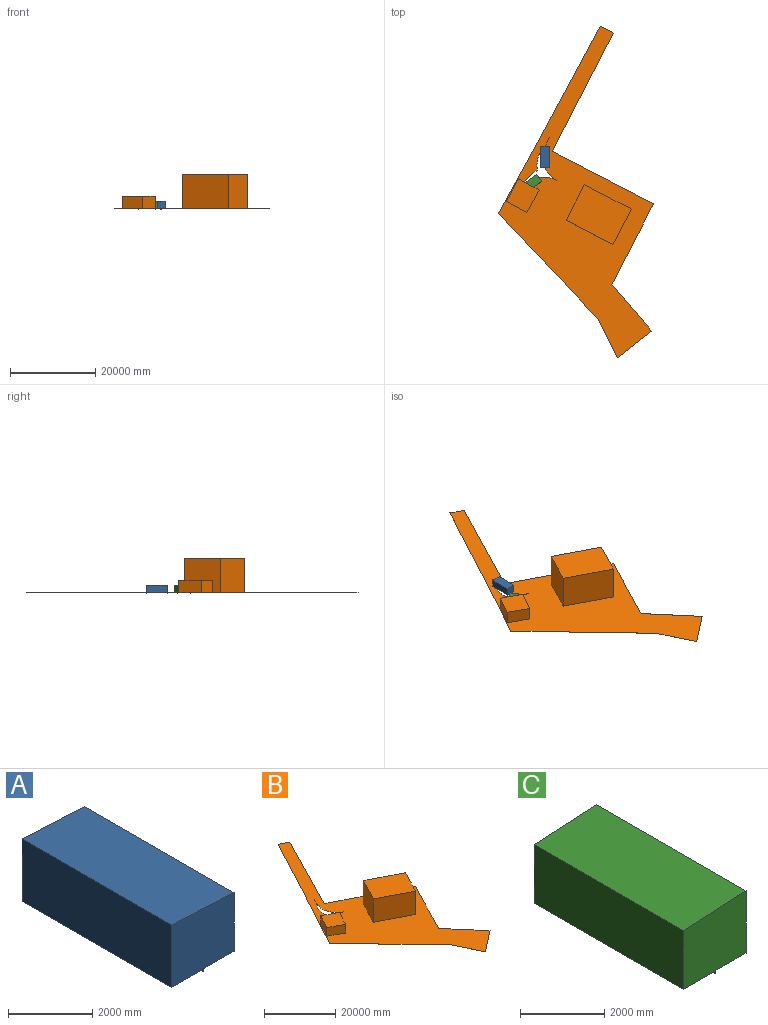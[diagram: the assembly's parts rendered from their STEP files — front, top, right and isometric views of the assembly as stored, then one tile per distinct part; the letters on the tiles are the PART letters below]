
ASSEMBLY  parts=3 mates=2
PART A: 12 faces, bbox 2100x5020x1860.1 mm
  f0: plane 2100x1810.06mm, normal (0,-1,0), area 3685559.2mm2, adj f1,f3,f4,f5,f6
  f1: plane 5000x1700mm, normal (1,0,0), area 8500000mm2, adj f0,f2,f4,f5
  f2: plane 2100x1810.06mm, normal (0,1,0), area 3685559.2mm2, adj f1,f3,f4,f5,f11
  f3: plane 5000x1810.06mm, normal (-1,0,0), area 9050281.7mm2, adj f0,f2,f4,f5
  f4: plane 5000x2100mm, normal (0.05,0,1), area 10514409.6mm2, adj f0,f1,f2,f3
  f5: plane 5000x2100mm, normal (0,0,-1), area 10499685.8mm2, adj f0,f1,f2,f3,f7,f9
  f6: plane 20x10mm, normal (0,0,1), area 157.1mm2, adj f0,f7
  f7: cylinder r=10mm len=50mm, axis (0,0,1), area 3141.6mm2, adj f5,f6,f8
  f8: plane 20x20mm, normal (0,0,-1), area 314.2mm2, adj f7
  f9: cylinder r=10mm len=50mm, axis (0,0,1), area 3141.6mm2, adj f5,f10,f11
  f10: plane 20x20mm, normal (0,0,-1), area 314.2mm2, adj f9
  f11: plane 20x10mm, normal (0,0,1), area 157.1mm2, adj f2,f9
PART B: 36 faces, bbox 36480.2x78044.6x8005 mm
  f0: plane 78044.58x36480.23mm, normal (0,0,1), area 819877426.7mm2, adj f2,f3,f4,f5,f6,f7,f8,f9
  f1: plane 78044.58x36480.23mm, normal (0,0,-1), area 968303998.2mm2, adj f2,f3,f4,f5,f6,f7,f8,f9
  f2: plane 27682.43x14769.46mm, normal (-0.88,0.47,0), area 156880mm2, adj f0,f1,f3,f11
  f3: plane 16564.67x9013.23mm, normal (-0.88,0.48,0), area 94290.3mm2, adj f0,f1,f2,f4
  f4: plane 24646.07x23560.1mm, normal (-0.72,-0.69,0), area 170477.8mm2, adj f0,f1,f3,f5
  f5: plane 9151.42x4420.6mm, normal (-0.9,-0.43,0), area 50815.9mm2, adj f0,f1,f4,f6
  f6: plane 8143.21x6359.46mm, normal (0.62,-0.79,0), area 51661.1mm2, adj f0,f1,f5,f7
  f7: plane 10935.17x9384.08mm, normal (0.76,0.65,0), area 72048.4mm2, adj f0,f1,f6,f8
  f8: plane 18967.71x9740.4mm, normal (0.89,-0.46,0), area 106612.6mm2, adj f0,f1,f7,f9
  f9: plane 23911.22x12274.5mm, normal (0.46,0.89,0), area 134388.4mm2, adj f0,f1,f8,f10
  f10: plane 27860.2x14301.66mm, normal (0.89,-0.46,0), area 156582.9mm2, adj f0,f1,f9,f11
  f11: plane 3087.98x1647.54mm, normal (0.47,0.88,0), area 17500mm2, adj f0,f1,f2,f10
  f12: plane 5270.32x3000mm, normal (0.88,-0.48,0), area 18000000mm2, adj f0,f13,f15,f16
  f13: plane 4831.13x3000mm, normal (0.48,0.88,0), area 16500000mm2, adj f0,f12,f14,f16,f27
  f14: plane 5270.32x3000mm, normal (-0.88,0.48,0), area 18000000mm2, adj f0,f13,f15,f16
  f15: plane 4831.13x3000mm, normal (-0.48,-0.88,0), area 16500000mm2, adj f0,f12,f14,f16
  f16: plane 7899.05x7698.83mm, normal (0,0,1), area 33000000mm2, adj f12,f13,f14,f15
  f17: plane 8341.3x8000mm, normal (0.89,-0.46,0), area 75014828.3mm2, adj f0,f18,f20,f21
  f18: plane 11032.67x8000mm, normal (0.46,0.89,0), area 99211211.4mm2, adj f0,f17,f19,f21
  f19: plane 8340.29x8000mm, normal (-0.89,0.46,0), area 75000000mm2, adj f0,f18,f20,f21
  f20: plane 11030.58x8000mm, normal (-0.46,-0.89,0), area 99200000mm2, adj f0,f17,f19,f21
  f21: plane 15314.05x14004.77mm, normal (0,0,1), area 116268061.2mm2, adj f17,f18,f19,f20
  f22: cylinder r=6000mm len=8010.4mm, axis (0,0,1), area 46402.1mm2, adj f0,f1,f23,f27,f28
  f23: plane 2034.22x1106.87mm, normal (-0.88,0.48,0), area 11579.3mm2, adj f1,f22,f24,f27
  f24: plane 17.57x9.56mm, normal (0.48,0.88,0), area 100mm2, adj f1,f23,f25,f27
  f25: plane 2034.22x1106.87mm, normal (0.88,-0.48,0), area 11579.3mm2, adj f1,f24,f26,f27
  f26: cylinder r=6000mm len=4748.25mm, axis (0,0,1), area 31154.3mm2, adj f0,f1,f25,f27,f33
  f27: plane 4001.33x2388.92mm, normal (0,0,-1), area 841489.8mm2, adj f13,f22,f23,f24,f25,f26
  f28: plane 8.9x5mm, normal (0.46,0.89,0), area 50mm2, adj f0,f1,f22,f29
  f29: plane 17.79x9.13mm, normal (-0.89,0.46,0), area 100mm2, adj f0,f1,f28,f30
  f30: plane 8.9x5mm, normal (-0.46,-0.89,0), area 50mm2, adj f0,f1,f29,f31
  f31: cylinder r=6000mm len=7948.65mm, axis (0,0,1), area 46402.1mm2, adj f0,f1,f30,f32
  f32: plane 2085.11x1007.74mm, normal (-0.9,0.44,0), area 11579.3mm2, adj f0,f1,f31,f34
  f33: cylinder r=6000mm len=5687.42mm, axis (0,0,1), area 31154.3mm2, adj f0,f1,f26,f35
  f34: plane 18.01x8.7mm, normal (-0.44,-0.9,0), area 100mm2, adj f0,f1,f32,f35
  f35: plane 2085.11x1007.74mm, normal (0.9,-0.44,0), area 11579.3mm2, adj f0,f1,f33,f34
PART C: 12 faces, bbox 2100x5020x1860.1 mm
  f0: plane 2100x1810.06mm, normal (0,-1,0), area 3685559.2mm2, adj f1,f3,f4,f5,f6
  f1: plane 5000x1810.06mm, normal (1,0,0), area 9050281.7mm2, adj f0,f2,f4,f5
  f2: plane 2100x1810.06mm, normal (0,1,0), area 3685559.2mm2, adj f1,f3,f4,f5,f11
  f3: plane 5000x1700mm, normal (-1,0,0), area 8500000mm2, adj f0,f2,f4,f5
  f4: plane 5000x2100mm, normal (-0.05,0,1), area 10514409.6mm2, adj f0,f1,f2,f3
  f5: plane 5000x2100mm, normal (0,0,-1), area 10499685.8mm2, adj f0,f1,f2,f3,f7,f9
  f6: plane 20x10mm, normal (0,0,1), area 157.1mm2, adj f0,f7
  f7: cylinder r=10mm len=50mm, axis (0,0,1), area 3141.6mm2, adj f5,f6,f8
  f8: plane 20x20mm, normal (0,0,-1), area 314.2mm2, adj f7
  f9: cylinder r=10mm len=50mm, axis (0,0,1), area 3141.6mm2, adj f5,f10,f11
  f10: plane 20x20mm, normal (0,0,-1), area 314.2mm2, adj f9
  f11: plane 20x10mm, normal (0,0,1), area 157.1mm2, adj f2,f9
PLACE A rot(axis=(0,0,1),179deg) t=(-17304.35,-10233.42,-686.7)mm
PLACE B rot(axis=(0,0,-1),0.2deg) t=(568.62,900.75,-691.7)mm fixed
PLACE C rot(axis=(0,0,-1),53.6deg) t=(-20618.74,-16678.83,-686.7)mm
MATE planar A.f5 <-> B.f0  axis (0,0,-1) through (-17304.35,-10233.42,-686.7)mm
MATE planar C.f5 <-> B.f0  axis (0,0,-1) through (-20618.74,-16678.83,-686.7)mm
